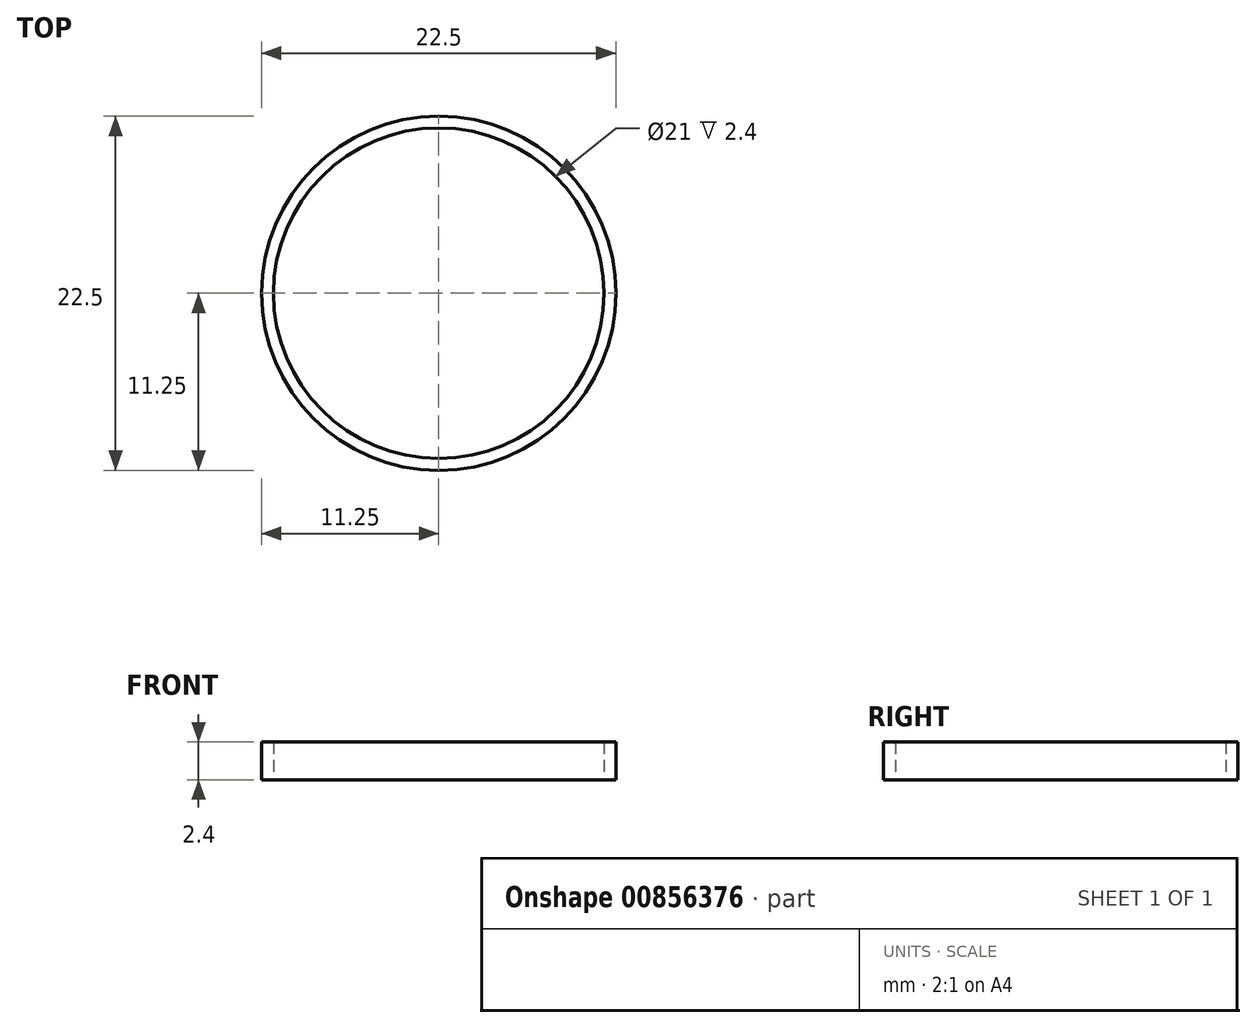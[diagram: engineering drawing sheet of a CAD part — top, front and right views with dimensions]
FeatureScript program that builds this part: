
annotation { "Feature Type Name" : "Feature", "Feature Type Description" : "" }
export const myFeature = defineFeature(function(context is Context, id is Id, definition is map)
    precondition{}
    {
        {
            var Q0;
            Q0=qCreatedBy(makeId("Top.planeOp"),FACE);
            var sketch = newSketch(context, id + "F0", { "sketchPlane" : qUnion([Q0])});
            skCircle(sketch, "E0", {"center": v(0, 0) * mm, "radius": 11.25 * mm});
            skCircle(sketch, "E1", {"center": v(0, 0) * mm, "radius": 10.5 * mm});
            skSolve(sketch);
        }
        {
            var Q0;
            Q0 = qSketchRegion(id + "F0", true);
            extrude(context, id + "F1", {"entities" : qUnion([Q0]), "depth" : 2.4 * mm, "offsetDistance" : 25 * mm});
        }
    });
